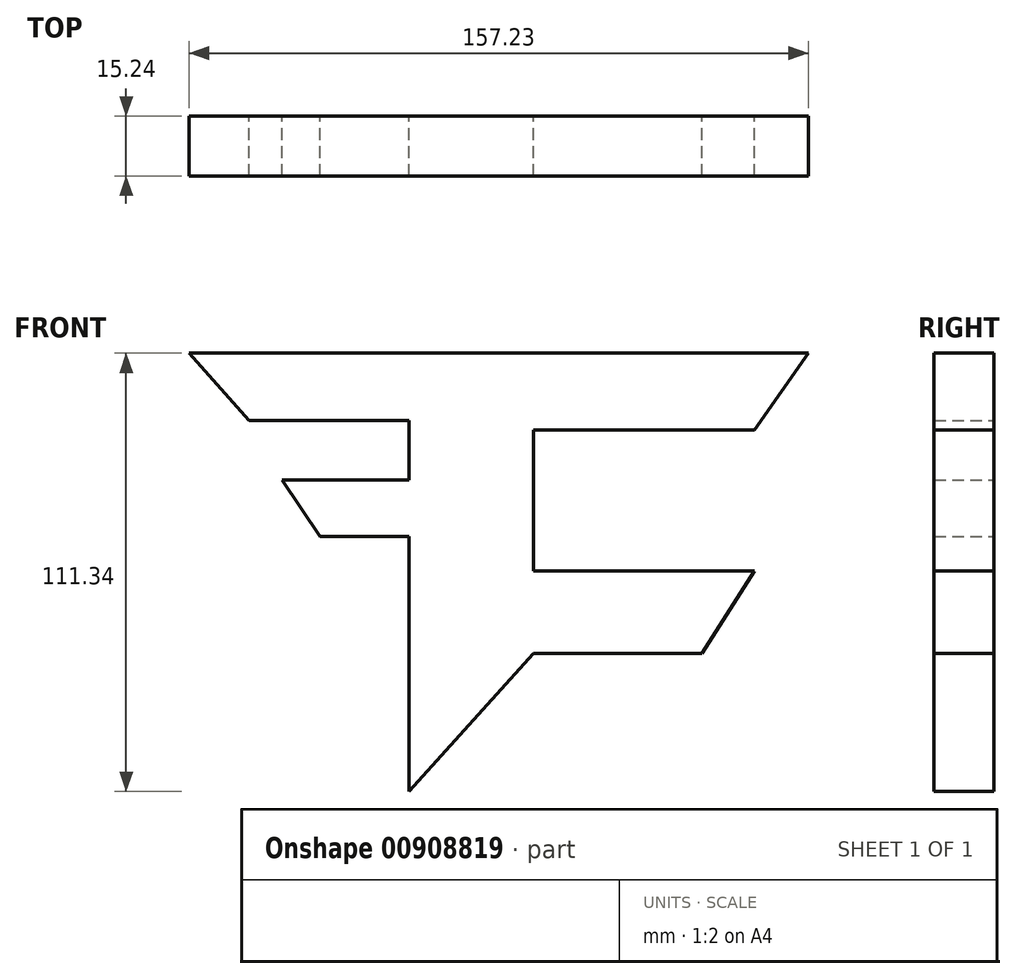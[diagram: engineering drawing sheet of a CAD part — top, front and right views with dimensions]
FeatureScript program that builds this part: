
annotation { "Feature Type Name" : "Feature", "Feature Type Description" : "" }
export const myFeature = defineFeature(function(context is Context, id is Id, definition is map)
    precondition{}
    {
        {
            var Q0;
            Q0=qCreatedBy(makeId("Front.planeOp"),FACE);
            var sketch = newSketch(context, id + "F0", { "sketchPlane" : qUnion([Q0])});
            skLineSegment(sketch, "E0", {"start": v(-60.32, 38.3) * mm, "end": v(-60.32, 23.1) * mm});
            skLineSegment(sketch, "E1", {"start": v(-60.32, 23.1) * mm, "end": v(-92.57, 23.1) * mm});
            skLineSegment(sketch, "E2", {"start": v(-100.94, 38.3) * mm, "end": v(-60.32, 38.3) * mm});
            skLineSegment(sketch, "E3", {"start": v(-100.94, 38.3) * mm, "end": v(-116.14, 55.36) * mm});
            skLineSegment(sketch, "E4", {"start": v(-116.14, 55.36) * mm, "end": v(41.1, 55.36) * mm});
            skLineSegment(sketch, "E5", {"start": v(41.1, 55.36) * mm, "end": v(27.45, 35.82) * mm});
            skLineSegment(sketch, "E6", {"start": v(27.45, 35.82) * mm, "end": v(-28.69, 35.82) * mm});
            skLineSegment(sketch, "E7", {"start": v(-28.69, 35.82) * mm, "end": v(-28.69, 0) * mm});
            skLineSegment(sketch, "E8", {"start": v(-28.69, 0) * mm, "end": v(27.45, 0) * mm});
            skLineSegment(sketch, "E9", {"start": v(27.45, 0) * mm, "end": v(14.11, -20.93) * mm});
            skLineSegment(sketch, "E10", {"start": v(14.11, -20.93) * mm, "end": v(-28.69, -20.93) * mm});
            skLineSegment(sketch, "E11", {"start": v(-28.69, -20.93) * mm, "end": v(-60.32, -55.98) * mm});
            skLineSegment(sketch, "E12", {"start": v(-60.32, -55.98) * mm, "end": v(-60.32, 8.84) * mm});
            skLineSegment(sketch, "E13", {"start": v(-60.32, 8.84) * mm, "end": v(-82.96, 8.84) * mm});
            skLineSegment(sketch, "E14", {"start": v(-82.96, 8.84) * mm, "end": v(-92.57, 23.1) * mm});
            skSolve(sketch);
        }
        {
            var Q0;
            Q0=makeQuery(id+"F0.imprint","IMPRINT",FACE,{"disambiguationData":[TD([[makeQuery(id+"F0.imprint","IMPRINT",EDGE,{"derivedFrom":sQuery(id+"F0.wireOp",EDGE,"E0")}),1.0]])]});
            extrude(context, id + "F1", {"entities" : qUnion([Q0]), "depth" : 15.24 * mm, "offsetDistance" : 25.4 * mm});
        }
    });
